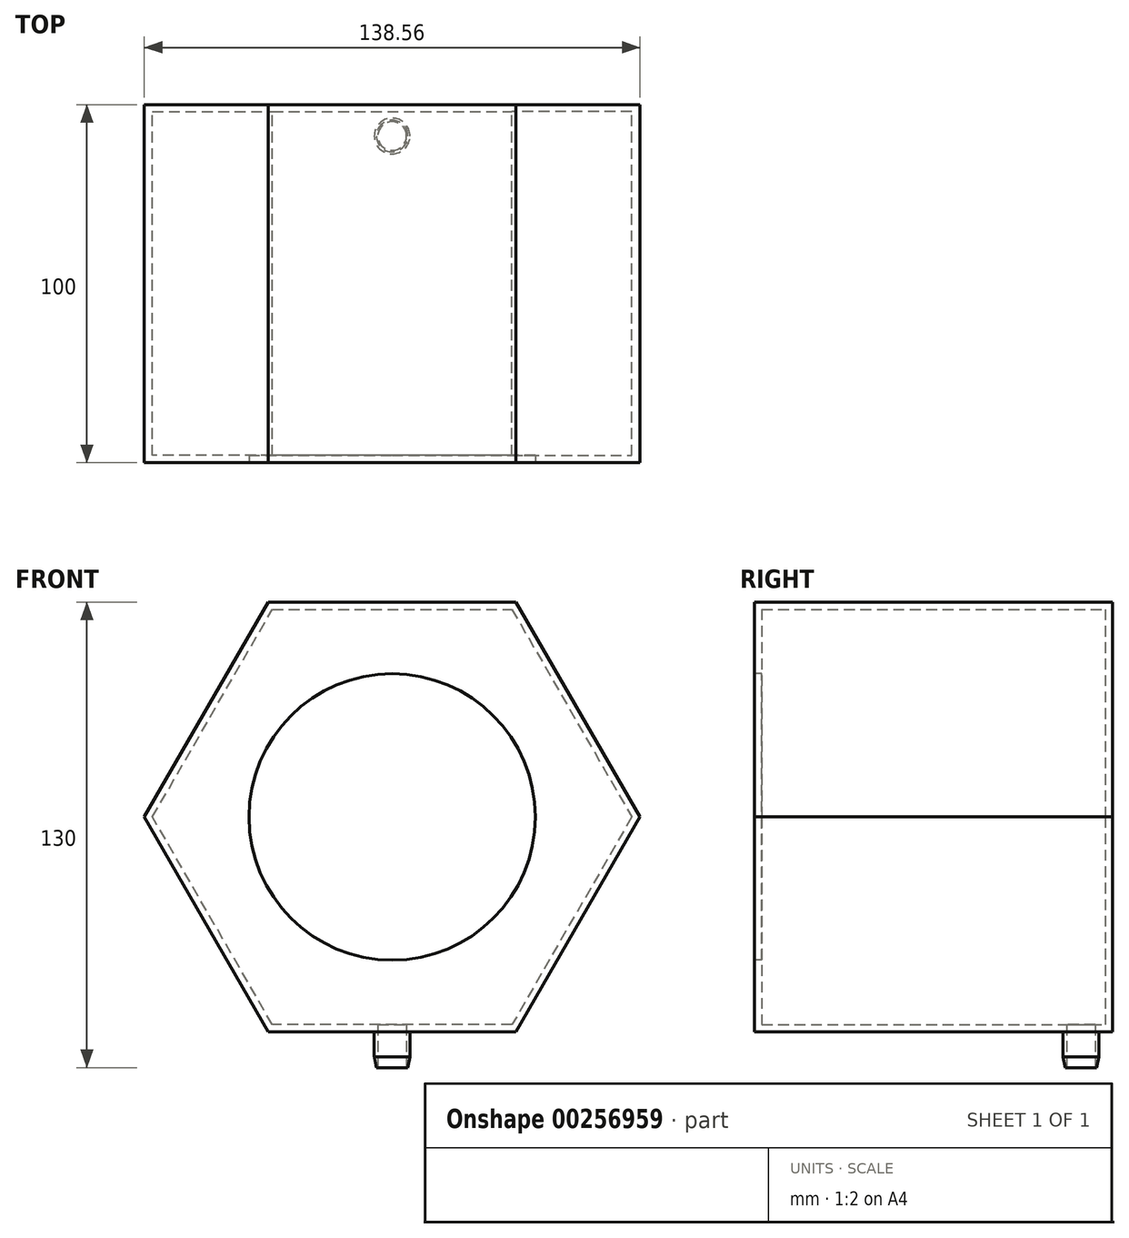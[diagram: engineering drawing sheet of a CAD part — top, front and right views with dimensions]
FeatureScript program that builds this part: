
annotation { "Feature Type Name" : "Feature", "Feature Type Description" : "" }
export const myFeature = defineFeature(function(context is Context, id is Id, definition is map)
    precondition{}
    {
        {
            var Q0;
            Q0=qCreatedBy(makeId("Front.planeOp"),FACE);
            var sketch = newSketch(context, id + "F0", { "sketchPlane" : qUnion([Q0])});
            skCircle(sketch, "E0.cCircle", {"center": v(0, 0) * mm, "radius": 60 * mm, "construction": true});
            skLineSegment(sketch, "E0.0", {"start": v(69.28, 0) * mm, "end": v(34.64, -60) * mm});
            skLineSegment(sketch, "E0.1", {"start": v(34.64, -60) * mm, "end": v(-34.64, -60) * mm});
            skLineSegment(sketch, "E0.2", {"start": v(-34.64, -60) * mm, "end": v(-69.28, 0) * mm});
            skLineSegment(sketch, "E0.3", {"start": v(-69.28, 0) * mm, "end": v(-34.64, 60) * mm});
            skLineSegment(sketch, "E0.4", {"start": v(-34.64, 60) * mm, "end": v(34.64, 60) * mm});
            skLineSegment(sketch, "E0.5", {"start": v(34.64, 60) * mm, "end": v(69.28, 0) * mm});
            skPoint(sketch, "E0.0.midPoint", {"position": v(51.96, -30) * mm});
            skSolve(sketch);
        }
        {
            var Q0;
            Q0=makeQuery(id+"F0.imprint","IMPRINT",FACE,{"disambiguationData":[TD([[makeQuery(id+"F0.imprint","IMPRINT",EDGE,{"derivedFrom":sQuery(id+"F0.wireOp",EDGE,"E0.0")}),-1.0]])]});
            extrude(context, id + "F1", {"entities" : qUnion([Q0]), "depth" : 100 * mm});
        }
        {
            var Q0;
            Q0=makeQuery(id+"F1.opExtrude","CAP_FACE",FACE,{"disambiguationData":[OSD([sQuery(id+"F0.wireOp",EDGE,"E0.0"),sQuery(id+"F0.wireOp",EDGE,"E0.1"),sQuery(id+"F0.wireOp",EDGE,"E0.2"),sQuery(id+"F0.wireOp",EDGE,"E0.3"),sQuery(id+"F0.wireOp",EDGE,"E0.4"),sQuery(id+"F0.wireOp",EDGE,"E0.5")])],"isStart":false});
            shell(context, id + "F2", {"entities" : qUnion([Q0]), "thickness" : 2 * mm});
        }
        {
            var Q0;
            Q0=makeQuery(id+"F1.opExtrude","CAP_FACE",FACE,{"disambiguationData":[OSD([sQuery(id+"F0.wireOp",EDGE,"E0.0"),sQuery(id+"F0.wireOp",EDGE,"E0.1"),sQuery(id+"F0.wireOp",EDGE,"E0.2"),sQuery(id+"F0.wireOp",EDGE,"E0.3"),sQuery(id+"F0.wireOp",EDGE,"E0.4"),sQuery(id+"F0.wireOp",EDGE,"E0.5")])],"isStart":false});
            var sketch = newSketch(context, id + "F3", { "sketchPlane" : qUnion([Q0])});
            skCircle(sketch, "E1", {"center": v(0, 0) * mm, "radius": 40 * mm});
            skSolve(sketch);
        }
        {
            var Q0;
            Q0=makeQuery(id+"F3.imprint","IMPRINT",FACE,{"disambiguationData":[TD([[makeQuery(id+"F3.imprint","IMPRINT",EDGE,{"derivedFrom":sQuery(id+"F3.wireOp",EDGE,"E1")}),-1.0]])]});
            extrude(context, id + "F4", {"entities" : qUnion([Q0]), "operationType" : NewBodyOperationType.ADD, "oppositeDirection" : true, "depth" : 2 * mm});
        }
        {
            var Q0;
            Q0=makeQuery(id+"F1.opExtrude","SWEPT_FACE",FACE,{"disambiguationData":[OSD([sQuery(id+"F0.wireOp",EDGE,"E0.1")])]});
            var sketch = newSketch(context, id + "F5", { "sketchPlane" : qUnion([Q0])});
            skCircle(sketch, "E2", {"center": v(0, 8.8) * mm, "radius": 4 * mm});
            skCircle(sketch, "E3", {"center": v(0, 8.8) * mm, "radius": 5 * mm});
            skSolve(sketch);
        }
        {
            var Q0;
            Q0=makeQuery(id+"F5.imprint","IMPRINT",FACE,{"disambiguationData":[TD([[makeQuery(id+"F5.imprint","IMPRINT",EDGE,{"derivedFrom":sQuery(id+"F5.wireOp",EDGE,"E2")}),1.0]])]});
            extrude(context, id + "F6", {"entities" : qUnion([Q0]), "operationType" : NewBodyOperationType.REMOVE, "endBound" : BoundingType.UP_TO_NEXT, "oppositeDirection" : true, "depth" : 25 * mm});
        }
        {
            var Q0;
            Q0=makeQuery(id+"F5.imprint","IMPRINT",FACE,{"disambiguationData":[TD([[makeQuery(id+"F5.imprint","IMPRINT",EDGE,{"derivedFrom":sQuery(id+"F5.wireOp",EDGE,"E2")}),-1.0]])]});
            extrude(context, id + "F7", {"entities" : qUnion([Q0]), "operationType" : NewBodyOperationType.ADD, "depth" : 10 * mm});
        }
        {
            var Q0;
            Q0=makeQuery(id+"F7.opExtrude","CAP_EDGE",EDGE,{"disambiguationData":[OSD([sQuery(id+"F5.wireOp",EDGE,"E3")])],"isStart":false});
            chamfer(context, id + "F8", {"entities" : qUnion([Q0]), "chamferType" : ChamferType.TWO_OFFSETS, "width1" : 0.6 * mm, "oppositeDirection" : false, "width2" : 3 * mm, "tangentPropagation" : true});
        }
    });
